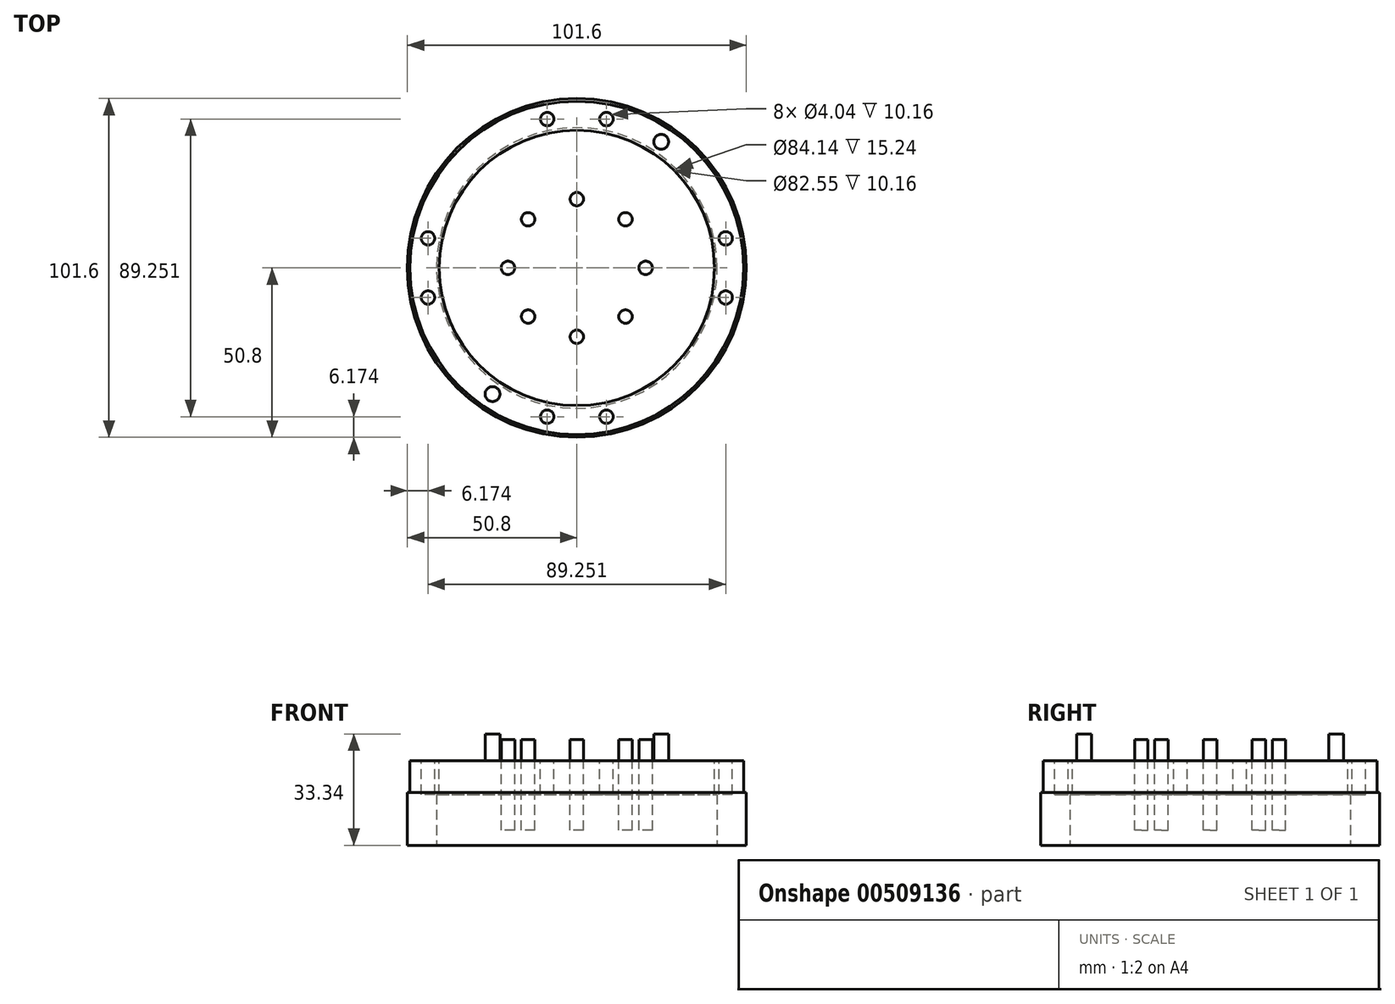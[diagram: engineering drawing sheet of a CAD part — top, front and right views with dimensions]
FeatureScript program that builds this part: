
annotation { "Feature Type Name" : "Feature", "Feature Type Description" : "" }
export const myFeature = defineFeature(function(context is Context, id is Id, definition is map)
    precondition{}
    {
        {
            var Q0;
            Q0=qCreatedBy(makeId("Top.planeOp"),FACE);
            var sketch = newSketch(context, id + "F0", { "sketchPlane" : qUnion([Q0])});
            skCircle(sketch, "E0", {"center": v(0, 0) * mm, "radius": 50.8 * mm});
            skCircle(sketch, "E1", {"center": v(0, 0) * mm, "radius": 50 * mm});
            skCircle(sketch, "E2", {"center": v(0, 0) * mm, "radius": 31.75 * mm});
            skSolve(sketch);
        }
        {
            var Q0;
            Q0 = qSketchRegion(id + "F0", true);
            var Q1;
            Q1=makeQuery(id+"F0.imprint","IMPRINT",FACE,{"disambiguationData":[TD([[makeQuery(id+"F0.imprint","IMPRINT",EDGE,{"derivedFrom":sQuery(id+"F0.wireOp",EDGE,"E1")}),1.0]])]});
            extrude(context, id + "F1", {"entities" : qUnion([Q0, Q1]), "depth" : 15.88 * mm});
        }
        {
            var Q0;
            Q0=makeQuery(id+"F0.imprint","IMPRINT",FACE,{"disambiguationData":[TD([[makeQuery(id+"F0.imprint","IMPRINT",EDGE,{"derivedFrom":sQuery(id+"F0.wireOp",EDGE,"E1")}),1.0]])]});
            extrude(context, id + "F2", {"entities" : qUnion([Q0]), "operationType" : NewBodyOperationType.ADD, "depth" : 25.4 * mm});
        }
        {
            var Q0;
            Q0=makeQuery(id+"F2.opExtrude","CAP_FACE",FACE,{"disambiguationData":[OSD([sQuery(id+"F0.wireOp",EDGE,"E1"),sQuery(id+"F0.wireOp",EDGE,"E2")])],"isStart":false});
            var sketch = newSketch(context, id + "F3", { "sketchPlane" : qUnion([Q0])});
            skSolve(sketch);
        }
        {
            var Q0;
            Q0=makeQuery(id+"F1.opExtrude","CAP_FACE",FACE,{"disambiguationData":[OSD([sQuery(id+"F0.wireOp",EDGE,"E0"),sQuery(id+"F0.wireOp",EDGE,"E2")])],"isStart":true});
            var sketch = newSketch(context, id + "F4", { "sketchPlane" : qUnion([Q0])});
            skCircle(sketch, "E3", {"center": v(0, 0) * mm, "radius": 42.07 * mm});
            skSolve(sketch);
        }
        {
            var Q0;
            Q0 = qSketchRegion(id + "F4", true);
            extrude(context, id + "F5", {"entities" : qUnion([Q0]), "operationType" : NewBodyOperationType.REMOVE, "oppositeDirection" : true, "depth" : 15.24 * mm});
        }
        {
            var Q0;
            Q0=makeQuery(id+"F3.imprint","IMPRINT",FACE,{"disambiguationData":[TD([[makeQuery(id+"F3.imprint","IMPRINT",EDGE,{"derivedFrom":makeQuery(id+"F2.opExtrude","CAP_EDGE",EDGE,{"disambiguationData":[OSD([sQuery(id+"F0.wireOp",EDGE,"E1")])],"isStart":false})}),1.0]])]});
            var sketch = newSketch(context, id + "F6", { "sketchPlane" : qUnion([Q0])});
            skCircle(sketch, "E4", {"center": v(44.63, 8.88) * mm, "radius": 2.02 * mm});
            skCircle(sketch, "E5", {"center": v(-44.63, -8.88) * mm, "radius": 2.02 * mm});
            skLineSegment(sketch, "E6", {"start": v(0, 0) * mm, "end": v(-44.63, -8.88) * mm});
            skLineSegment(sketch, "E7", {"start": v(0, 0) * mm, "end": v(44.63, 8.88) * mm});
            skLineSegment(sketch, "E8", {"start": v(0, 0) * mm, "end": v(12.7, 0) * mm});
            skCircle(sketch, "E9", {"center": v(44.63, -8.88) * mm, "radius": 2.02 * mm});
            skLineSegment(sketch, "E10", {"start": v(0, 0) * mm, "end": v(44.63, -8.88) * mm});
            skLineSegment(sketch, "E11", {"start": v(0, 0) * mm, "end": v(-12.7, 0) * mm});
            skCircle(sketch, "E12", {"center": v(-44.63, 8.88) * mm, "radius": 2.02 * mm});
            skLineSegment(sketch, "E13", {"start": v(-44.63, 8.88) * mm, "end": v(0, 0) * mm});
            skLineSegment(sketch, "E14", {"start": v(0, 0) * mm, "end": v(0, 12.7) * mm});
            skLineSegment(sketch, "E15", {"start": v(0, 0) * mm, "end": v(0, -12.7) * mm});
            skCircle(sketch, "E16", {"center": v(-8.88, 44.63) * mm, "radius": 2.02 * mm});
            skLineSegment(sketch, "E17", {"start": v(0, 0) * mm, "end": v(-8.88, 44.63) * mm});
            skCircle(sketch, "E18", {"center": v(8.88, 44.63) * mm, "radius": 2.02 * mm});
            skLineSegment(sketch, "E19", {"start": v(8.88, 44.63) * mm, "end": v(0, 0) * mm});
            skCircle(sketch, "E20", {"center": v(-8.88, -44.63) * mm, "radius": 2.02 * mm});
            skCircle(sketch, "E21", {"center": v(8.88, -44.63) * mm, "radius": 2.02 * mm});
            skLineSegment(sketch, "E22", {"start": v(0, 0) * mm, "end": v(-8.88, -44.63) * mm});
            skLineSegment(sketch, "E23", {"start": v(8.88, -44.63) * mm, "end": v(0, 0) * mm});
            skSolve(sketch);
        }
        {
            var Q0;
            Q0 = qSketchRegion(id + "F6", true);
            extrude(context, id + "F7", {"entities" : qUnion([Q0]), "operationType" : NewBodyOperationType.REMOVE, "oppositeDirection" : true, "depth" : 10.16 * mm});
        }
        {
            var Q0;
            Q0=makeQuery(id+"F5.boolean.opBoolean","COPY",FACE,{"derivedFrom":makeQuery(id+"F5.opExtrude","CAP_FACE",FACE,{"disambiguationData":[OSD([sQuery(id+"F4.wireOp",EDGE,"E3")])],"isStart":false})});
            cPlane(context, id + "F8", {"entities" : qUnion([Q0]), "cplaneType" : CPlaneType.OFFSET, "offset" : 0.25 * mm, "width" : 152.4 * mm, "height" : 152.4 * mm});
        }
        {
            var Q0;
            Q0=qCreatedBy(id+"F8.planeOp",FACE);
            var sketch = newSketch(context, id + "F9", { "sketchPlane" : qUnion([Q0])});
            skCircle(sketch, "E24", {"center": v(0, 0) * mm, "radius": 41.28 * mm});
            skCircle(sketch, "E25", {"center": v(0, 0) * mm, "radius": 11.11 * mm});
            skSolve(sketch);
        }
        {
            var Q0;
            Q0 = qSketchRegion(id + "F9", true);
            extrude(context, id + "F10", {"entities" : qUnion([Q0]), "depth" : 10.48 * mm});
        }
        {
            var Q0;
            Q0=qCreatedBy(id+"F8.planeOp",FACE);
            var sketch = newSketch(context, id + "F11", { "sketchPlane" : qUnion([Q0])});
            skCircle(sketch, "E26", {"center": v(0, 0) * mm, "radius": 31.62 * mm});
            skCircle(sketch, "E27", {"center": v(0, 0) * mm, "radius": 11.11 * mm});
            skSolve(sketch);
        }
        {
            var Q0;
            Q0 = qSketchRegion(id + "F11", true);
            extrude(context, id + "F12", {"entities" : qUnion([Q0]), "operationType" : NewBodyOperationType.ADD, "oppositeDirection" : true, "depth" : 10.67 * mm});
        }
        {
            var Q0;
            Q0=makeQuery(id+"F12.opExtrude","CAP_FACE",FACE,{"disambiguationData":[OSD([sQuery(id+"F11.wireOp",EDGE,"E26"),sQuery(id+"F11.wireOp",EDGE,"E27")])],"isStart":false});
            var sketch = newSketch(context, id + "F13", { "sketchPlane" : qUnion([Q0])});
            skCircle(sketch, "E28", {"center": v(0, 0) * mm, "radius": 11.11 * mm});
            skCircle(sketch, "E29", {"center": v(0, 0) * mm, "radius": 41.28 * mm});
            skSolve(sketch);
        }
        {
            var Q0;
            Q0 = qSketchRegion(id + "F13", true);
            extrude(context, id + "F14", {"entities" : qUnion([Q0]), "operationType" : NewBodyOperationType.ADD, "depth" : 9.27 * mm});
        }
        {
            var Q0;
            Q0=makeQuery(id+"F14.opExtrude","CAP_FACE",FACE,{"disambiguationData":[OSD([sQuery(id+"F13.wireOp",EDGE,"E28"),sQuery(id+"F13.wireOp",EDGE,"E29")])],"isStart":false});
            var sketch = newSketch(context, id + "F15", { "sketchPlane" : qUnion([Q0])});
            skCircle(sketch, "E30.cCircle", {"center": v(0, 0) * mm, "radius": 20.64 * mm, "construction": true});
            skLineSegment(sketch, "E30.0", {"start": v(-8.55, 20.64) * mm, "end": v(8.55, 20.64) * mm});
            skLineSegment(sketch, "E30.1", {"start": v(8.55, 20.64) * mm, "end": v(20.64, 8.55) * mm});
            skLineSegment(sketch, "E30.2", {"start": v(20.64, 8.55) * mm, "end": v(20.64, -8.55) * mm});
            skLineSegment(sketch, "E30.3", {"start": v(20.64, -8.55) * mm, "end": v(8.55, -20.64) * mm});
            skLineSegment(sketch, "E30.4", {"start": v(8.55, -20.64) * mm, "end": v(-8.55, -20.64) * mm});
            skLineSegment(sketch, "E30.5", {"start": v(-8.55, -20.64) * mm, "end": v(-20.64, -8.55) * mm});
            skLineSegment(sketch, "E30.6", {"start": v(-20.64, -8.55) * mm, "end": v(-20.64, 8.55) * mm});
            skLineSegment(sketch, "E30.7", {"start": v(-20.64, 8.55) * mm, "end": v(-8.55, 20.64) * mm});
            skPoint(sketch, "E30.0.midPoint", {"position": v(0, 20.64) * mm});
            skCircle(sketch, "E31", {"center": v(-14.6, 14.6) * mm, "radius": 2.02 * mm});
            skCircle(sketch, "E32", {"center": v(0, 20.64) * mm, "radius": 2.02 * mm});
            skCircle(sketch, "E33", {"center": v(14.6, 14.6) * mm, "radius": 2.02 * mm});
            skCircle(sketch, "E34", {"center": v(-20.64, 0) * mm, "radius": 2.02 * mm});
            skCircle(sketch, "E35", {"center": v(-14.6, -14.6) * mm, "radius": 2.02 * mm});
            skCircle(sketch, "E36", {"center": v(0, -20.64) * mm, "radius": 2.02 * mm});
            skCircle(sketch, "E37", {"center": v(14.6, -14.6) * mm, "radius": 2.02 * mm});
            skCircle(sketch, "E38", {"center": v(20.64, 0) * mm, "radius": 2.02 * mm});
            skSolve(sketch);
        }
        {
            var Q0;
            {var subQ0=sQuery(id+"F15.wireOp",EDGE,"E32");var subQ1=sQuery(id+"F15.wireOp",EDGE,"E30.0");var subQ2=makeQuery(id+"F15.imprint","INTERSECT",VERTEX,{"disambiguationData":[OD(0.0)],"derivedFrom":[subQ1,subQ0]});Q0=makeQuery(id+"F15.imprint","IMPRINT",FACE,{"disambiguationData":[TD([[makeQuery(id+"F15.imprint","IMPRINT",EDGE,{"disambiguationData":[TD([[subQ2,-1.0]])],"derivedFrom":subQ1}),1.0]])]});}
            var Q1;
            {var subQ0=sQuery(id+"F15.wireOp",EDGE,"E32");var subQ1=sQuery(id+"F15.wireOp",EDGE,"E30.0");var subQ2=makeQuery(id+"F15.imprint","INTERSECT",VERTEX,{"disambiguationData":[OD(0.0)],"derivedFrom":[subQ1,subQ0]});Q1=makeQuery(id+"F15.imprint","IMPRINT",FACE,{"disambiguationData":[TD([[makeQuery(id+"F15.imprint","IMPRINT",EDGE,{"disambiguationData":[TD([[subQ2,-1.0]])],"derivedFrom":subQ1}),-1.0]])]});}
            var Q2;
            {var subQ0=sQuery(id+"F15.wireOp",EDGE,"E33");var subQ1=sQuery(id+"F15.wireOp",EDGE,"E30.1");var subQ2=makeQuery(id+"F15.imprint","INTERSECT",VERTEX,{"disambiguationData":[OD(0.0)],"derivedFrom":[subQ1,subQ0]});Q2=makeQuery(id+"F15.imprint","IMPRINT",FACE,{"disambiguationData":[TD([[makeQuery(id+"F15.imprint","IMPRINT",EDGE,{"disambiguationData":[TD([[subQ2,-1.0]])],"derivedFrom":subQ1}),-1.0]])]});}
            var Q3;
            {var subQ0=sQuery(id+"F15.wireOp",EDGE,"E33");var subQ1=sQuery(id+"F15.wireOp",EDGE,"E30.1");var subQ2=makeQuery(id+"F15.imprint","INTERSECT",VERTEX,{"disambiguationData":[OD(0.0)],"derivedFrom":[subQ1,subQ0]});Q3=makeQuery(id+"F15.imprint","IMPRINT",FACE,{"disambiguationData":[TD([[makeQuery(id+"F15.imprint","IMPRINT",EDGE,{"disambiguationData":[TD([[subQ2,-1.0]])],"derivedFrom":subQ1}),1.0]])]});}
            var Q4;
            {var subQ0=sQuery(id+"F15.wireOp",EDGE,"E38");var subQ1=sQuery(id+"F15.wireOp",EDGE,"E30.2");var subQ2=makeQuery(id+"F15.imprint","INTERSECT",VERTEX,{"disambiguationData":[OD(0.0)],"derivedFrom":[subQ1,subQ0]});Q4=makeQuery(id+"F15.imprint","IMPRINT",FACE,{"disambiguationData":[TD([[makeQuery(id+"F15.imprint","IMPRINT",EDGE,{"disambiguationData":[TD([[subQ2,-1.0]])],"derivedFrom":subQ1}),-1.0]])]});}
            var Q5;
            {var subQ0=sQuery(id+"F15.wireOp",EDGE,"E38");var subQ1=sQuery(id+"F15.wireOp",EDGE,"E30.2");var subQ2=makeQuery(id+"F15.imprint","INTERSECT",VERTEX,{"disambiguationData":[OD(0.0)],"derivedFrom":[subQ1,subQ0]});Q5=makeQuery(id+"F15.imprint","IMPRINT",FACE,{"disambiguationData":[TD([[makeQuery(id+"F15.imprint","IMPRINT",EDGE,{"disambiguationData":[TD([[subQ2,-1.0]])],"derivedFrom":subQ1}),1.0]])]});}
            var Q6;
            {var subQ0=sQuery(id+"F15.wireOp",EDGE,"E37");var subQ1=sQuery(id+"F15.wireOp",EDGE,"E30.3");var subQ2=makeQuery(id+"F15.imprint","INTERSECT",VERTEX,{"disambiguationData":[OD(0.0)],"derivedFrom":[subQ1,subQ0]});Q6=makeQuery(id+"F15.imprint","IMPRINT",FACE,{"disambiguationData":[TD([[makeQuery(id+"F15.imprint","IMPRINT",EDGE,{"disambiguationData":[TD([[subQ2,-1.0]])],"derivedFrom":subQ1}),-1.0]])]});}
            var Q7;
            {var subQ0=sQuery(id+"F15.wireOp",EDGE,"E37");var subQ1=sQuery(id+"F15.wireOp",EDGE,"E30.3");var subQ2=makeQuery(id+"F15.imprint","INTERSECT",VERTEX,{"disambiguationData":[OD(0.0)],"derivedFrom":[subQ1,subQ0]});Q7=makeQuery(id+"F15.imprint","IMPRINT",FACE,{"disambiguationData":[TD([[makeQuery(id+"F15.imprint","IMPRINT",EDGE,{"disambiguationData":[TD([[subQ2,-1.0]])],"derivedFrom":subQ1}),1.0]])]});}
            var Q8;
            {var subQ0=sQuery(id+"F15.wireOp",EDGE,"E36");var subQ1=sQuery(id+"F15.wireOp",EDGE,"E30.4");var subQ2=makeQuery(id+"F15.imprint","INTERSECT",VERTEX,{"disambiguationData":[OD(0.0)],"derivedFrom":[subQ1,subQ0]});Q8=makeQuery(id+"F15.imprint","IMPRINT",FACE,{"disambiguationData":[TD([[makeQuery(id+"F15.imprint","IMPRINT",EDGE,{"disambiguationData":[TD([[subQ2,-1.0]])],"derivedFrom":subQ1}),-1.0]])]});}
            var Q9;
            {var subQ0=sQuery(id+"F15.wireOp",EDGE,"E36");var subQ1=sQuery(id+"F15.wireOp",EDGE,"E30.4");var subQ2=makeQuery(id+"F15.imprint","INTERSECT",VERTEX,{"disambiguationData":[OD(0.0)],"derivedFrom":[subQ1,subQ0]});Q9=makeQuery(id+"F15.imprint","IMPRINT",FACE,{"disambiguationData":[TD([[makeQuery(id+"F15.imprint","IMPRINT",EDGE,{"disambiguationData":[TD([[subQ2,-1.0]])],"derivedFrom":subQ1}),1.0]])]});}
            var Q10;
            {var subQ0=sQuery(id+"F15.wireOp",EDGE,"E35");var subQ1=sQuery(id+"F15.wireOp",EDGE,"E30.5");var subQ2=makeQuery(id+"F15.imprint","INTERSECT",VERTEX,{"disambiguationData":[OD(0.0)],"derivedFrom":[subQ1,subQ0]});Q10=makeQuery(id+"F15.imprint","IMPRINT",FACE,{"disambiguationData":[TD([[makeQuery(id+"F15.imprint","IMPRINT",EDGE,{"disambiguationData":[TD([[subQ2,-1.0]])],"derivedFrom":subQ1}),1.0]])]});}
            var Q11;
            {var subQ0=sQuery(id+"F15.wireOp",EDGE,"E35");var subQ1=sQuery(id+"F15.wireOp",EDGE,"E30.5");var subQ2=makeQuery(id+"F15.imprint","INTERSECT",VERTEX,{"disambiguationData":[OD(0.0)],"derivedFrom":[subQ1,subQ0]});Q11=makeQuery(id+"F15.imprint","IMPRINT",FACE,{"disambiguationData":[TD([[makeQuery(id+"F15.imprint","IMPRINT",EDGE,{"disambiguationData":[TD([[subQ2,-1.0]])],"derivedFrom":subQ1}),-1.0]])]});}
            var Q12;
            {var subQ0=sQuery(id+"F15.wireOp",EDGE,"E34");var subQ1=sQuery(id+"F15.wireOp",EDGE,"E30.6");var subQ2=makeQuery(id+"F15.imprint","INTERSECT",VERTEX,{"disambiguationData":[OD(0.0)],"derivedFrom":[subQ1,subQ0]});Q12=makeQuery(id+"F15.imprint","IMPRINT",FACE,{"disambiguationData":[TD([[makeQuery(id+"F15.imprint","IMPRINT",EDGE,{"disambiguationData":[TD([[subQ2,-1.0]])],"derivedFrom":subQ1}),1.0]])]});}
            var Q13;
            {var subQ0=sQuery(id+"F15.wireOp",EDGE,"E34");var subQ1=sQuery(id+"F15.wireOp",EDGE,"E30.6");var subQ2=makeQuery(id+"F15.imprint","INTERSECT",VERTEX,{"disambiguationData":[OD(0.0)],"derivedFrom":[subQ1,subQ0]});Q13=makeQuery(id+"F15.imprint","IMPRINT",FACE,{"disambiguationData":[TD([[makeQuery(id+"F15.imprint","IMPRINT",EDGE,{"disambiguationData":[TD([[subQ2,-1.0]])],"derivedFrom":subQ1}),-1.0]])]});}
            var Q14;
            {var subQ0=sQuery(id+"F15.wireOp",EDGE,"E31");var subQ1=sQuery(id+"F15.wireOp",EDGE,"E30.7");var subQ2=makeQuery(id+"F15.imprint","INTERSECT",VERTEX,{"disambiguationData":[OD(0.0)],"derivedFrom":[subQ1,subQ0]});Q14=makeQuery(id+"F15.imprint","IMPRINT",FACE,{"disambiguationData":[TD([[makeQuery(id+"F15.imprint","IMPRINT",EDGE,{"disambiguationData":[TD([[subQ2,-1.0]])],"derivedFrom":subQ1}),1.0]])]});}
            var Q15;
            {var subQ0=sQuery(id+"F15.wireOp",EDGE,"E31");var subQ1=sQuery(id+"F15.wireOp",EDGE,"E30.7");var subQ2=makeQuery(id+"F15.imprint","INTERSECT",VERTEX,{"disambiguationData":[OD(0.0)],"derivedFrom":[subQ1,subQ0]});Q15=makeQuery(id+"F15.imprint","IMPRINT",FACE,{"disambiguationData":[TD([[makeQuery(id+"F15.imprint","IMPRINT",EDGE,{"disambiguationData":[TD([[subQ2,-1.0]])],"derivedFrom":subQ1}),-1.0]])]});}
            extrude(context, id + "F16", {"entities" : qUnion([Q0, Q1, Q2, Q3, Q4, Q5, Q6, Q7, Q8, Q9, Q10, Q11, Q12, Q13, Q14, Q15]), "operationType" : NewBodyOperationType.REMOVE, "oppositeDirection" : true, "depth" : 50.8 * mm});
        }
        {
            var Q0;
            Q0=makeQuery(id+"F14.opExtrude","CAP_FACE",FACE,{"disambiguationData":[OSD([sQuery(id+"F13.wireOp",EDGE,"E28"),sQuery(id+"F13.wireOp",EDGE,"E29")])],"isStart":false});
            var sketch = newSketch(context, id + "F17", { "sketchPlane" : qUnion([Q0])});
            skCircle(sketch, "E39", {"center": v(-14.6, 14.6) * mm, "radius": 3.97 * mm});
            skCircle(sketch, "E40", {"center": v(-20.64, 0) * mm, "radius": 3.97 * mm});
            skCircle(sketch, "E41", {"center": v(-14.6, -14.6) * mm, "radius": 3.97 * mm});
            skCircle(sketch, "E42", {"center": v(0, -20.64) * mm, "radius": 3.97 * mm});
            skCircle(sketch, "E43", {"center": v(14.6, -14.6) * mm, "radius": 3.97 * mm});
            skCircle(sketch, "E44", {"center": v(20.64, 0) * mm, "radius": 3.97 * mm});
            skCircle(sketch, "E45", {"center": v(14.6, 14.6) * mm, "radius": 3.97 * mm});
            skCircle(sketch, "E46", {"center": v(0, 20.64) * mm, "radius": 3.97 * mm});
            skSolve(sketch);
        }
        {
            var Q0;
            Q0 = qSketchRegion(id + "F17", true);
            extrude(context, id + "F18", {"entities" : qUnion([Q0]), "operationType" : NewBodyOperationType.REMOVE, "oppositeDirection" : true, "depth" : 3.17 * mm});
        }
        {
            var Q0;
            Q0=makeQuery(id+"F3.imprint","IMPRINT",FACE,{"disambiguationData":[TD([[makeQuery(id+"F3.imprint","IMPRINT",EDGE,{"derivedFrom":makeQuery(id+"F2.opExtrude","CAP_EDGE",EDGE,{"disambiguationData":[OSD([sQuery(id+"F0.wireOp",EDGE,"E1")])],"isStart":false})}),1.0]])]});
            var sketch = newSketch(context, id + "F19", { "sketchPlane" : qUnion([Q0])});
            skCircle(sketch, "E47", {"center": v(-25.28, -37.83) * mm, "radius": 2.22 * mm});
            skCircle(sketch, "E48", {"center": v(25.28, 37.83) * mm, "radius": 2.22 * mm});
            skLineSegment(sketch, "E49", {"start": v(0, 0) * mm, "end": v(0, 12.7) * mm});
            skLineSegment(sketch, "E50", {"start": v(0, 0) * mm, "end": v(25.28, 37.83) * mm});
            skLineSegment(sketch, "E51", {"start": v(0, 0) * mm, "end": v(-25.28, -37.83) * mm});
            skLineSegment(sketch, "E52", {"start": v(0, 0) * mm, "end": v(0, -12.7) * mm});
            skSolve(sketch);
        }
        {
            var Q0;
            Q0 = qSketchRegion(id + "F19", true);
            extrude(context, id + "F20", {"entities" : qUnion([Q0]), "operationType" : NewBodyOperationType.ADD, "depth" : 7.94 * mm});
        }
    });
